# Revit family: ASH_ArmitageShanks_WallHungHandRinseBasins_Portman21-500mm
name_source: partatom
category: Plumbing Fixtures
revit_build: Autodesk Revit MEP 2012 (Build: 20110309_2315(x64)
units: mm (PartAtom-declared; Revit-internal decimal feet)

## types (8) — shared parameters
Accessories = www.idealspec.co.uk
AreaUnits = millimeters
Assembly Code = C1030200
AssetType = Fixed
BREEAMApproved = Yes
Brand = Armitage Shanks
CodePerformance = Vitreous china to bs 3402.   washbasin to bs en 14688 & bs en 31
Color = White
ConnectionType = Plumbing
Default Elevation = 1219 mm
DrainSize = 32 mm  [stored 0.104987 ft]
DurationUnit = year
ECA = Yes
ExpectedLife = 30
Finish = White
Help = www.idealspec.co.uk/contact-us.html
IfcExportAs = IfcSanitaryTerminalType
IfcExportType = WASHHANDBASIN
InstallationInstructions = www.idealspec.co.uk/resources.html
LinearUnits = millimeters
ManufacturerURL = www.idealspec.co.uk
Material = Vitreous china
NBSDescription = Wall hung hand rinse basins
NBSReference = 45-35-70/368
Name = WallHungHandRinseBasins_Portman21_50cm_ArmitageShanks
NettWeight = 12.7 Kg
NominalDepth = 420 mm  [stored 1.37795 ft]
NominalHeight = 195 mm  [stored 0.639764 ft]
NominalLength = 420 mm  [stored 1.37795 ft]
NominalWidth = 500 mm  [stored 1.64042 ft]
Shape = Sculptured
Size = 500 x 420 x 195 mm
Space = Internal
URL = www.idealspec.co.uk
Uniclass2 = Pr_40_20_96_96
Version = 2
VolumeUnits = Litres
WRAS = Yes
WarrantyDescription = Manufacturers Warranty
WarrantyDurationParts = 99
WarrantyDurationUnit = year
WashHandBasinMounting = WallHung
WashHandBasinType = HandRinse
WaterEfficientProduct = Yes
zero-valued in all types: CWFU, Cost, HWFU, WFU

## per-type parameters (varying)
| type | 1CTH | 1LHTH | 1RHTH | 2TH | BIMObjectName | Description | Features | Model | ModelNumber | ModelReference | NoTH | ProductInformation |
| S230901 - Portman 21 Washbasin 50cm 2 Taphole, Chainstay Hole & Overflow | No | No | No | Yes | ASH_ArmitageShanks_WallHungHandRinseBasins-Portman21-500mm_S2309 | Portman 21 washbasin 50 cm 2 taphole, chainstay hole & overflow | 50 cm 2 taphole, chainstay hole & overflow | S230901 | S230901 | Portman 21 washbasin 50 cm 2 taphole, chainstay hole & overflow | No | www.idealspec.co.uk/assets/datasheet/S230901 |
| S231001 - Portman 21 Washbasin 50cm 2 Taphole With Overflow No Chainstay Hole | No | No | No | Yes | ASH_ArmitageShanks_WallHungHandRinseBasins-Portman21-500mm_S2310 | Portman 21 washbasin 50 cm 2 taphole with overflow no chainstay hole | 50 cm 2 taphole with overflow no chainstay hole | S231001 | S231001 | Portman 21 washbasin 50 cm 2 taphole with overflow no chainstay hole | No | www.idealspec.co.uk/assets/datasheet/S231001 |
| S225301 - Portman 21 Washbasin 50cm 2 Taphole, No Overflow or Chainstay Hole | No | No | No | Yes | ASH_ArmitageShanks_WallHungHandRinseBasins-Portman21-500mm_S2253 | Portman 21 washbasin 50 cm 2 taphole, no overflow or chainstay hole | 50 cm 2 taphole, no overflow or chainstay hole | S225301 | S225301 | Portman 21 washbasin 50 cm 2 taphole, no overflow or chainstay hole | No | www.idealspec.co.uk/assets/datasheet/S225301 |
| S231101 - Portman 21 Washbasin 50cm Centre Taphole Overflow N o Chain | Yes | No | No | No | ASH_ArmitageShanks_WallHungHandRinseBasins-Portman21-500mm_S2311 | Portman 21 washbasin 50 cm centre taphole overflow n o chain | 50 cm centre taphole overflow n o chain | S231101 | S231101 | Portman 21 washbasin 50 cm centre taphole overflow n o chain | No | www.idealspec.co.uk/assets/datasheet/S231101 |
| S225101 - Portman 21 Washbasin 50cm No Taphole, Chainstay or Overflow | No | No | No | No | ASH_ArmitageShanks_WallHungHandRinseBasins-Portman21-500mm_S2251 | Portman 21 washbasin 50 cm no taphole, chainstay or overflow | 50 cm no taphole, chainstay or overflow | S225101 | S225101 | Portman 21 washbasin 50 cm no taphole, chainstay or overflow | Yes | www.idealspec.co.uk/assets/datasheet/S225101 |
| S230801 - Portman 21 Washbasin 50cm LH Taphole, No Overflow or Chainstay Hole | No | Yes | No | No | ASH_ArmitageShanks_WallHungHandRinseBasins-Portman21-500mm_S2308 | Portman 21 washbasin 50 cm lh taphole, no overflow or chainstay hole | 50 cm lh taphole, no overflow or chainstay hole | S230801 | S230801 | Portman 21 washbasin 50 cm lh taphole, no overflow or chainstay hole | No | www.idealspec.co.uk/assets/datasheet/S230801 |
| S225401 - Portman 21 Washbasin 50cm RH Taphole, No Overflow or Chainstay Hole | No | No | Yes | No | ASH_ArmitageShanks_WallHungHandRinseBasins-Portman21-500mm_S2254 | Portman 21 washbasin 50 cm rh taphole, no overflow or chainstay hole | 50 cm rh taphole, no overflow or chainstay hole | S225401 | S225401 | Portman 21 washbasin 50 cm rh taphole, no overflow or chainstay hole | No | www.idealspec.co.uk/assets/datasheet/S225401 |
| S225201 - Portman 21 Washbasin 50cm 1 Taphole No Overflow or Chainstay Hole | Yes | No | No | No | ASH_ArmitageShanks_WallHungHandRinseBasins-Portman21-500mm_S2252 | Portman 21 washbasin 50 cm 1 taphole no overflow or chainstay hole | 50 cm 1 taphole no overflow or chainstay hole | S225201 | S225201 | Portman 21 washbasin 50 cm 1 taphole no overflow or chainstay hole | No | www.idealspec.co.uk/assets/datasheet/S225201 |

note: [stored X ft] marks values corroborated as IEEE doubles in the binary element streams (Revit-internal decimal feet)

## geometry (parser evidence)
native form markers: Blend x5, Sweep x14
no freeform markers — native parametric forms only
